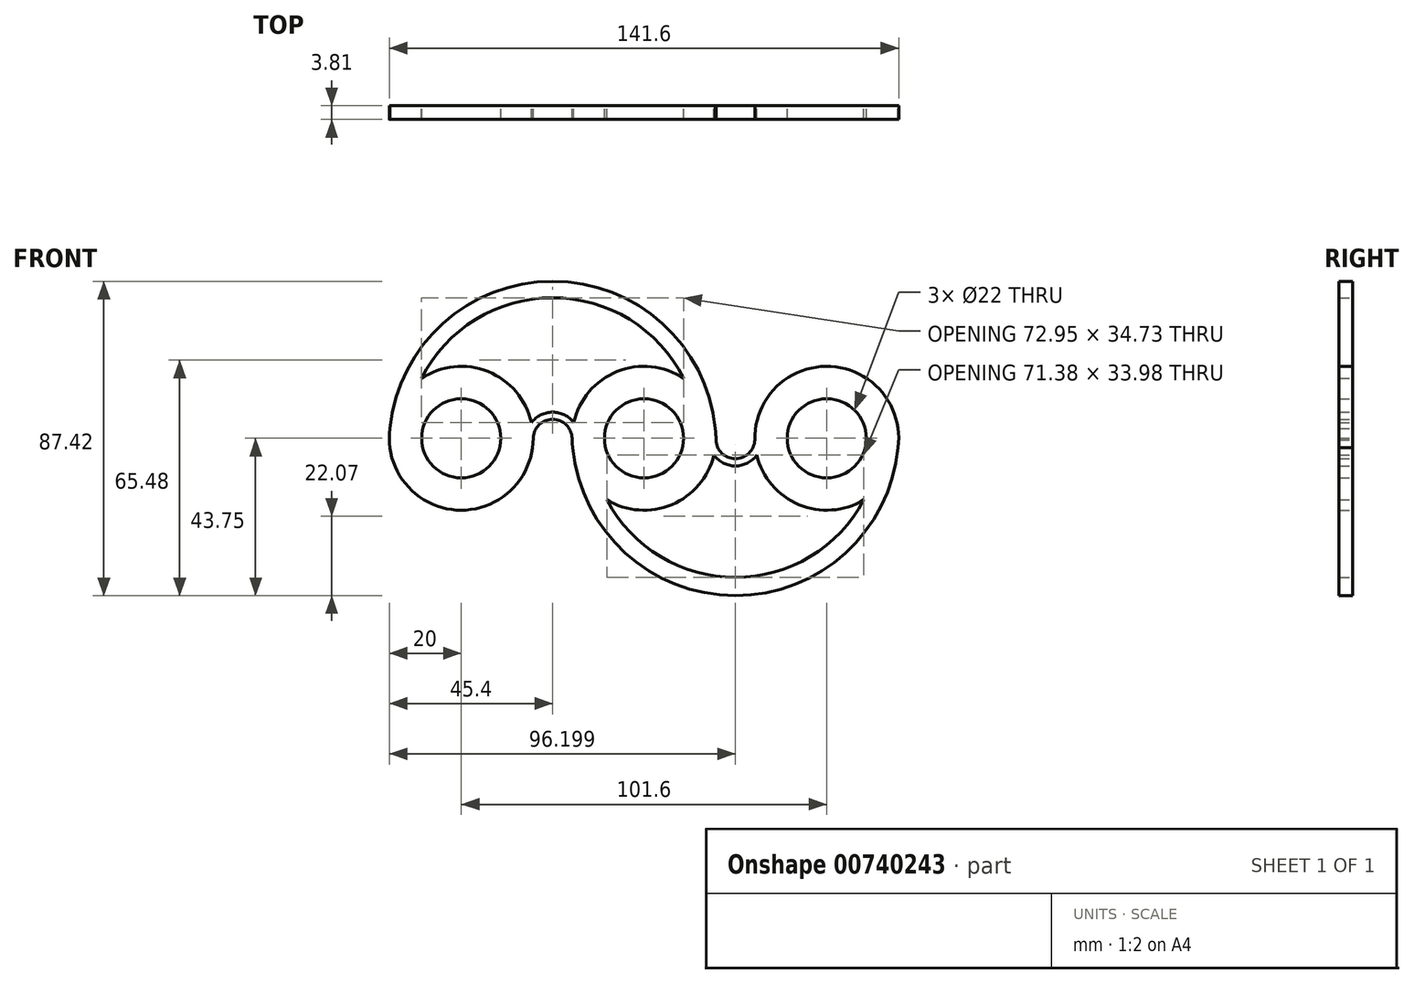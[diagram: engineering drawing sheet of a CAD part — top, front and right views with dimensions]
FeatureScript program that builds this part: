
annotation { "Feature Type Name" : "Feature", "Feature Type Description" : "" }
export const myFeature = defineFeature(function(context is Context, id is Id, definition is map)
    precondition{}
    {
        {
            var Q0;
            Q0=qCreatedBy(makeId("Front.planeOp"),FACE);
            var sketch = newSketch(context, id + "F0", { "sketchPlane" : qUnion([Q0])});
            skCircle(sketch, "E0", {"center": v(0, 0) * mm, "radius": 11 * mm});
            skCircle(sketch, "E1", {"center": v(0, 0) * mm, "radius": 4 * mm});
            skCircle(sketch, "E2", {"center": v(0, 0) * mm, "radius": 20 * mm});
            skCircle(sketch, "E3.1.0.0", {"center": v(50.8, 0) * mm, "radius": 4 * mm});
            skCircle(sketch, "E3.1.0.1", {"center": v(50.8, 0) * mm, "radius": 11 * mm});
            skCircle(sketch, "E3.1.0.2", {"center": v(50.8, 0) * mm, "radius": 20 * mm});
            skCircle(sketch, "E3.2.0.0", {"center": v(101.6, 0) * mm, "radius": 4 * mm});
            skCircle(sketch, "E3.2.0.1", {"center": v(101.6, 0) * mm, "radius": 11 * mm});
            skCircle(sketch, "E3.2.0.2", {"center": v(101.6, 0) * mm, "radius": 20 * mm});
            skLineSegment(sketch, "E3.direction1", {"start": v(0, 0) * mm, "end": v(50.8, 0) * mm, "construction": true});
            skArc(sketch, "E4", {"start": v(30.8, 0) * mm, "mid": v(25.4, 5.27) * mm, "end": v(20, 0) * mm});
            skArc(sketch, "E5.0", {"start": v(32.8, 0.05) * mm, "mid": v(25.4, 7.27) * mm, "end": v(18, 0.05) * mm});
            skArc(sketch, "E6", {"start": v(70.8, 0) * mm, "mid": v(76.2, -5.7) * mm, "end": v(81.6, 0) * mm});
            skArc(sketch, "E7.0", {"start": v(68.8, 0.1) * mm, "mid": v(76.17, -7.7) * mm, "end": v(83.6, 0.04) * mm});
            skArc(sketch, "E8", {"start": v(70.8, 0) * mm, "mid": v(25.4, 43.67) * mm, "end": v(-20, 0) * mm});
            skArc(sketch, "E9.0", {"start": v(66.23, -0.18) * mm, "mid": v(25.4, 39.1) * mm, "end": v(-15.43, -0.18) * mm});
            skArc(sketch, "E10", {"start": v(30.8, 0) * mm, "mid": v(76.22, -43.75) * mm, "end": v(121.6, 0.04) * mm});
            skArc(sketch, "E11.0", {"start": v(35.88, 0.16) * mm, "mid": v(76.31, -38.67) * mm, "end": v(116.53, 0.39) * mm});
            skArc(sketch, "E11.1", {"start": v(35.88, 0.16) * mm, "mid": v(25.38, 10.35) * mm, "end": v(14.92, 0.12) * mm});
            skSolve(sketch);
        }
        {
            var Q0;
            Q0 = qSketchRegion(id + "F0", true);
            extrude(context, id + "F1", {"entities" : qUnion([Q0]), "depth" : 3.8 * mm, "offsetDistance" : 25.4 * mm});
        }
    });
